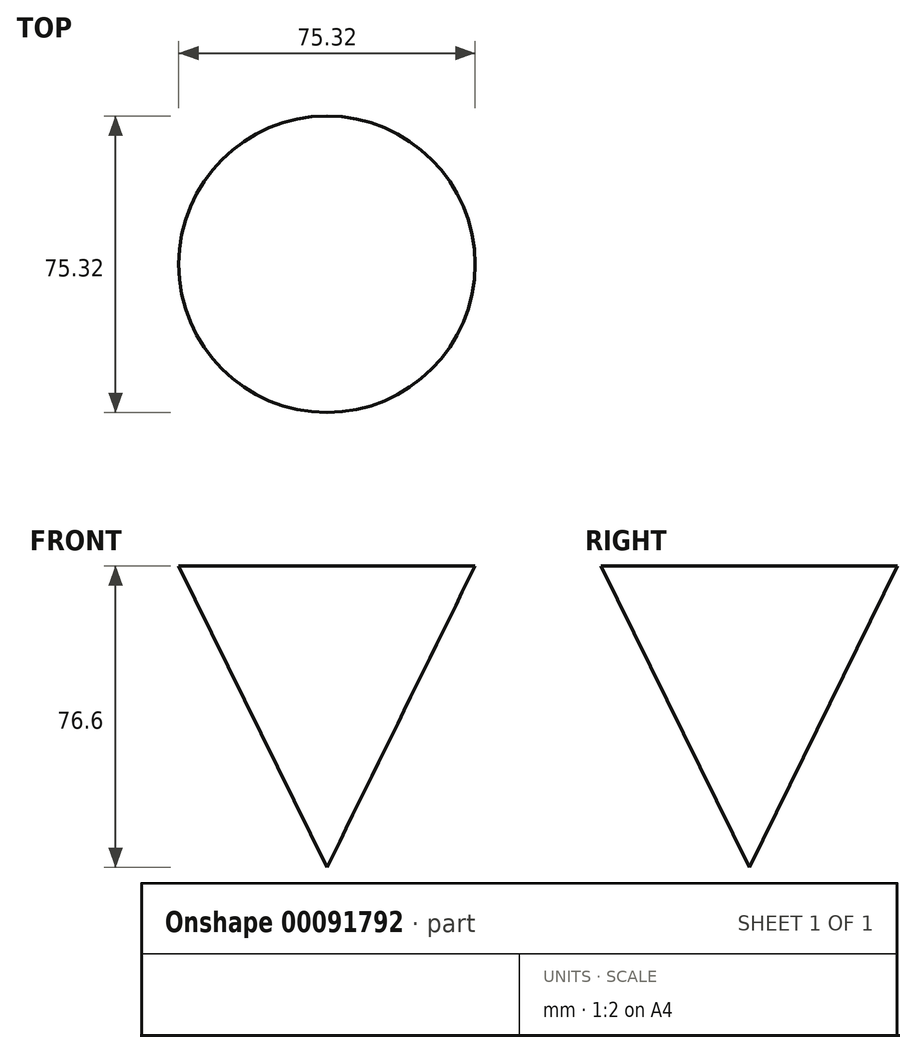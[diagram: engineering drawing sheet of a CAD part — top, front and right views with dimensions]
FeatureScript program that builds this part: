
annotation { "Feature Type Name" : "Feature", "Feature Type Description" : "" }
export const myFeature = defineFeature(function(context is Context, id is Id, definition is map)
    precondition{}
    {
        {
            var Q0;
            Q0=qCreatedBy(makeId("Front.planeOp"),FACE);
            var sketch = newSketch(context, id + "F0", { "sketchPlane" : qUnion([Q0])});
            skLineSegment(sketch, "E0", {"start": v(0, -76.6) * mm, "end": v(-37.66, 0) * mm});
            skLineSegment(sketch, "E1", {"start": v(-37.66, 0) * mm, "end": v(0, 0) * mm});
            skLineSegment(sketch, "E2", {"start": v(0, 0) * mm, "end": v(0, -76.6) * mm});
            skSolve(sketch);
        }
        {
            var Q0;
            Q0 = qSketchRegion(id + "F0", true);
            var Q1;
            Q1=sQuery(id+"F0.wireOp",EDGE,"E2");
            revolve(context, id + "F1", {"entities" : qUnion([Q0]), "axis" : qUnion([Q1]), "revolveType" : RevolveType.FULL});
        }
    });
